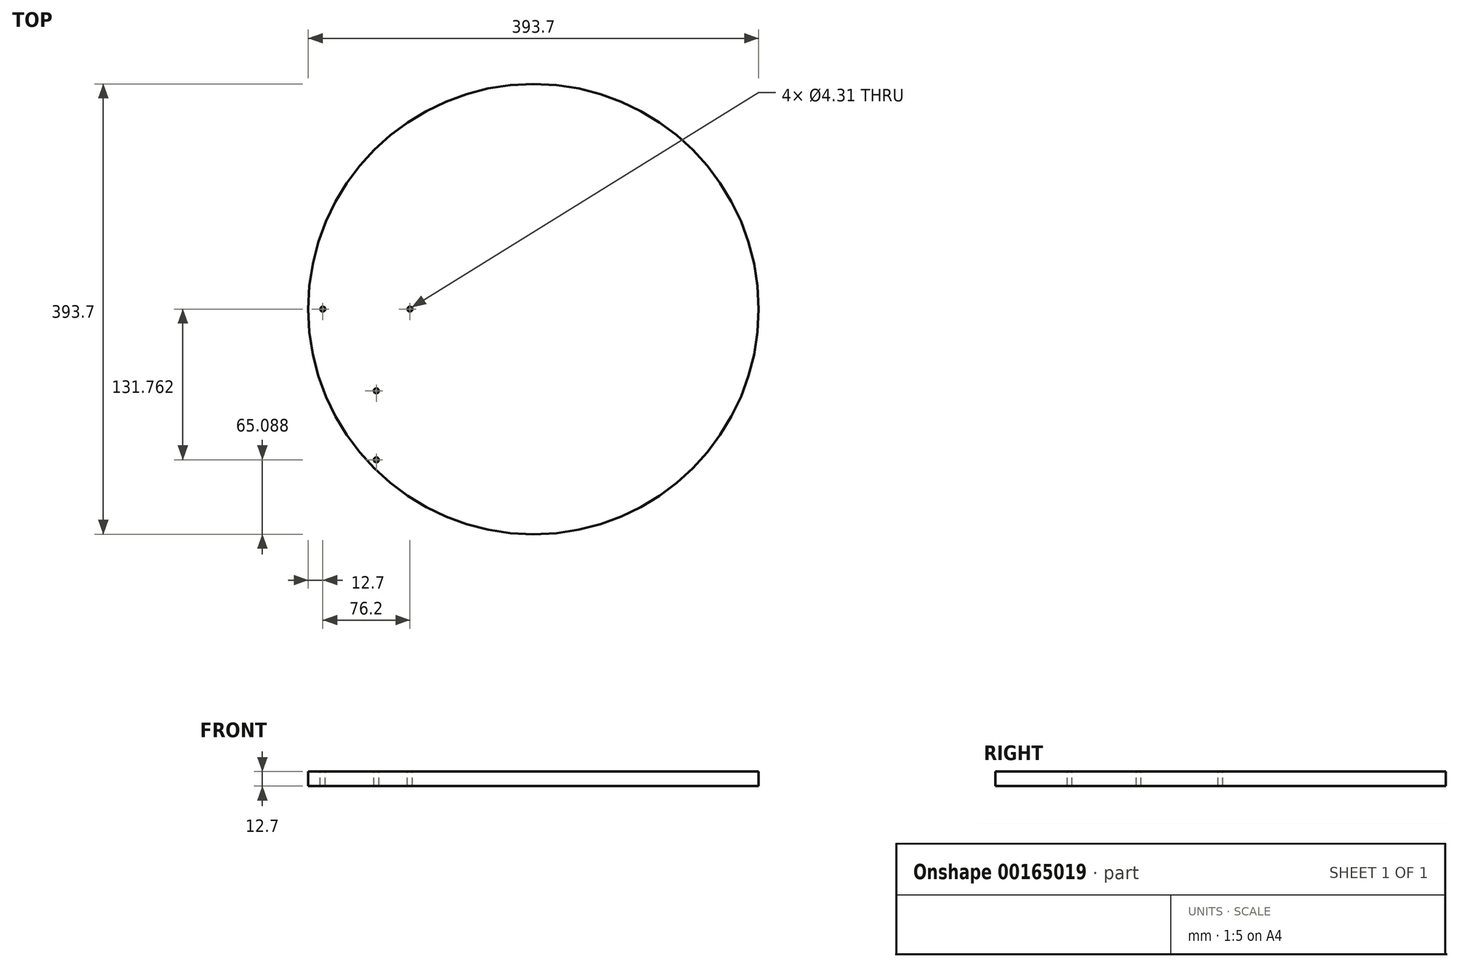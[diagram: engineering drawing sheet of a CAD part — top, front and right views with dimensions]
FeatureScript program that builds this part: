
annotation { "Feature Type Name" : "Feature", "Feature Type Description" : "" }
export const myFeature = defineFeature(function(context is Context, id is Id, definition is map)
    precondition{}
    {
        {
            var Q0;
            Q0=qCreatedBy(makeId("Top.planeOp"),FACE);
            var sketch = newSketch(context, id + "F0", { "sketchPlane" : qUnion([Q0])});
            skCircle(sketch, "E0", {"center": v(0, 0) * mm, "radius": 196.85 * mm});
            skSolve(sketch);
        }
        {
            var Q0;
            Q0=qSketchRegion(id+"F0",true);
            extrude(context, id + "F1", {"entities" : qUnion([Q0]), "depth" : 12.7 * mm});
        }
        {
            var Q0;
            Q0=makeQuery(id+"F1.opExtrude","CAP_FACE",FACE,{"disambiguationData":[OSD([sQuery(id+"F0.wireOp",EDGE,"E0")])],"isStart":false});
            var sketch = newSketch(context, id + "F2", { "sketchPlane" : qUnion([Q0])});
            skLineSegment(sketch, "E1", {"start": v(0, 0) * mm, "end": v(0, -101.6) * mm, "construction": true});
            skLineSegment(sketch, "E2", {"start": v(0, -101.6) * mm, "end": v(-167.48, -101.6) * mm, "construction": true});
            skLineSegment(sketch, "E3.bottom", {"start": v(-137.32, -131.76) * mm, "end": v(-197.64, -131.76) * mm, "construction": true});
            skLineSegment(sketch, "E3.top", {"start": v(-137.32, -71.44) * mm, "end": v(-197.64, -71.44) * mm, "construction": true});
            skLineSegment(sketch, "E3.left", {"start": v(-137.32, -131.76) * mm, "end": v(-137.32, -71.44) * mm, "construction": true});
            skLineSegment(sketch, "E3.right", {"start": v(-197.64, -131.76) * mm, "end": v(-197.64, -71.44) * mm, "construction": true});
            skPoint(sketch, "E3.middle", {"position": v(-167.48, -101.6) * mm});
            skCircle(sketch, "E4", {"center": v(-137.32, -71.44) * mm, "radius": 2.15 * mm});
            skCircle(sketch, "E5", {"center": v(-137.32, -131.76) * mm, "radius": 2.15 * mm});
            skCircle(sketch, "E6", {"center": v(-197.64, -71.44) * mm, "radius": 2.15 * mm});
            skCircle(sketch, "E7", {"center": v(-197.64, -131.76) * mm, "radius": 2.15 * mm});
            skLineSegment(sketch, "E8", {"start": v(0, 0) * mm, "end": v(-107.95, 0) * mm, "construction": true});
            skLineSegment(sketch, "E9", {"start": v(-107.95, 0) * mm, "end": v(-184.15, 0) * mm, "construction": true});
            skLineSegment(sketch, "E10", {"start": v(-184.15, 0) * mm, "end": v(-196.85, 0) * mm, "construction": true});
            skCircle(sketch, "E11", {"center": v(-107.95, 0) * mm, "radius": 2.15 * mm});
            skCircle(sketch, "E12", {"center": v(-184.15, 0) * mm, "radius": 2.15 * mm});
            skSolve(sketch);
        }
        {
            var Q0;
            Q0=qSketchRegion(id+"F2",true);
            var Q1;
            Q1=makeQuery(id+"F1.opExtrude","CAP_FACE",FACE,{"disambiguationData":[OSD([sQuery(id+"F0.wireOp",EDGE,"E0")])],"isStart":true});
            extrude(context, id + "F3", {"entities" : qUnion([Q0]), "operationType" : NewBodyOperationType.REMOVE, "endBound" : BoundingType.UP_TO_SURFACE, "oppositeDirection" : true, "endBoundEntityFace" : qUnion([Q1]), "depth" : 25.4 * mm});
        }
    });
